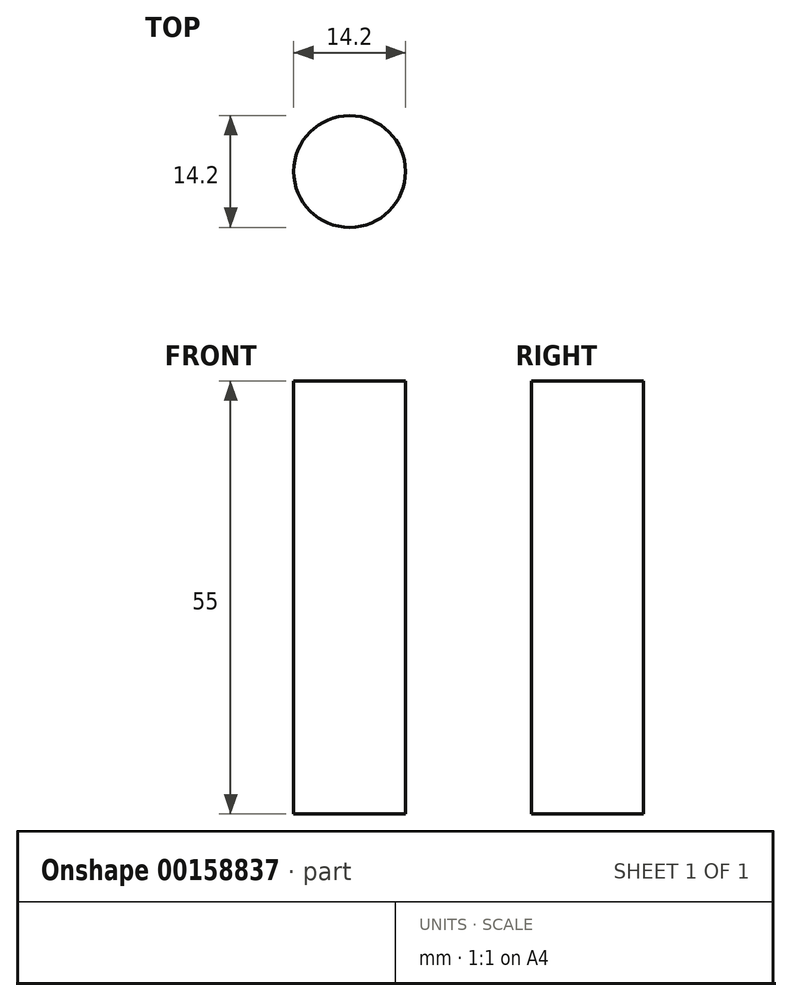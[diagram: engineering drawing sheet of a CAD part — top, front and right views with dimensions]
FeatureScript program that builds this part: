
annotation { "Feature Type Name" : "Feature", "Feature Type Description" : "" }
export const myFeature = defineFeature(function(context is Context, id is Id, definition is map)
    precondition{}
    {
        {
            var Q0;
            Q0=qCreatedBy(makeId("Top.planeOp"),FACE);
            var sketch = newSketch(context, id + "F0", { "sketchPlane" : qUnion([Q0])});
            skCircle(sketch, "E0", {"center": v(0, 0) * mm, "radius": 7.1 * mm});
            skSolve(sketch);
        }
        {
            var Q0;
            Q0 = qSketchRegion(id + "F0", true);
            extrude(context, id + "F1", {"entities" : qUnion([Q0]), "depth" : 55 * mm});
        }
    });
